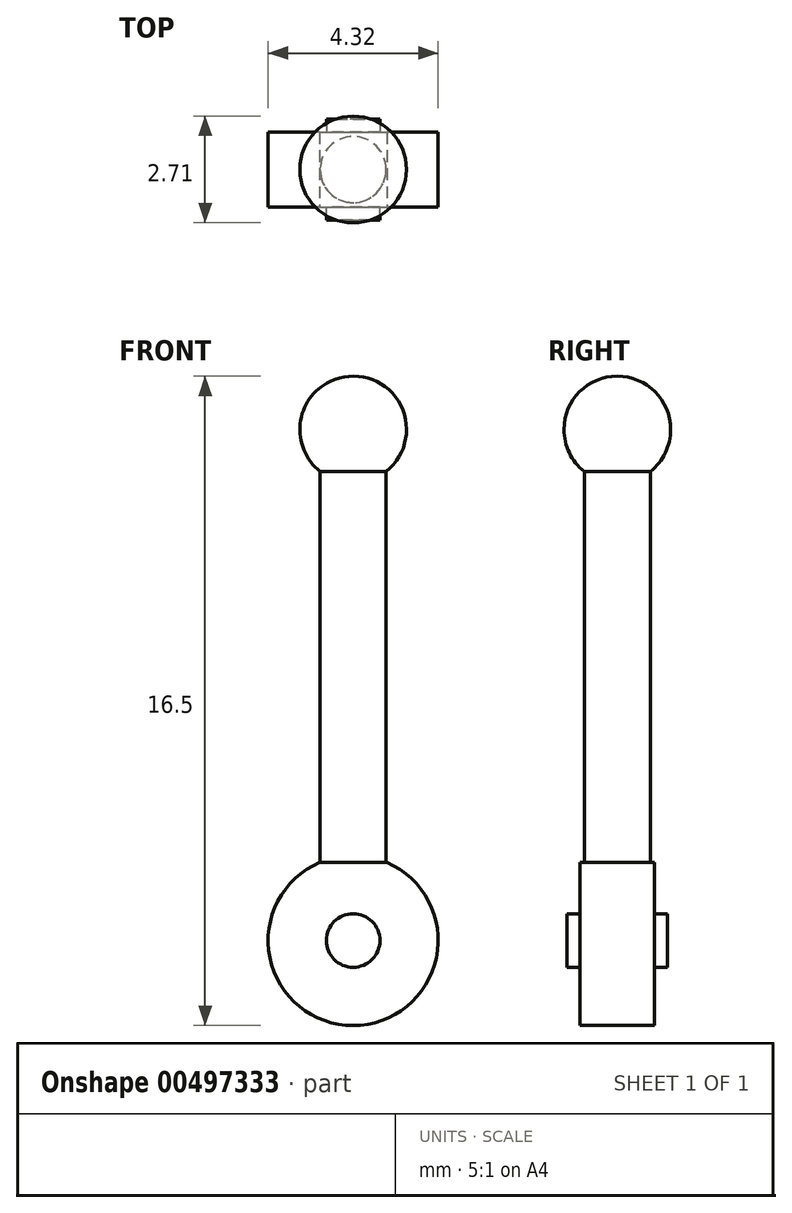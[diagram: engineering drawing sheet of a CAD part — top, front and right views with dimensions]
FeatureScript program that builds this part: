
annotation { "Feature Type Name" : "Feature", "Feature Type Description" : "" }
export const myFeature = defineFeature(function(context is Context, id is Id, definition is map)
    precondition{}
    {
        {
            var Q0;
            Q0=qCreatedBy(makeId("Front.planeOp"),FACE);
            var sketch = newSketch(context, id + "F0", { "sketchPlane" : qUnion([Q0])});
            skCircle(sketch, "E0", {"center": v(0, 0) * mm, "radius": 2.16 * mm});
            skSolve(sketch);
        }
        {
            var Q0;
            Q0 = qSketchRegion(id + "F0", true);
            extrude(context, id + "F1", {"entities" : qUnion([Q0]), "depth" : 1.9 * mm});
        }
        {
            var Q0;
            Q0=makeQuery(id+"F1.opExtrude","CAP_FACE",FACE,{"disambiguationData":[OSD([sQuery(id+"F0.wireOp",EDGE,"E0")])],"isStart":false});
            var sketch = newSketch(context, id + "F2", { "sketchPlane" : qUnion([Q0])});
            skLineSegment(sketch, "E1", {"start": v(-0.85, 1.98) * mm, "end": v(0.85, 1.98) * mm});
            skSolve(sketch);
        }
        {
            var Q0;
            Q0=makeQuery(id+"F1.opExtrude","CAP_FACE",FACE,{"disambiguationData":[OSD([sQuery(id+"F0.wireOp",EDGE,"E0")])],"isStart":true});
            var sketch = newSketch(context, id + "F3", { "sketchPlane" : qUnion([Q0])});
            skCircle(sketch, "E2", {"center": v(0, 0) * mm, "radius": 0.68 * mm});
            skSolve(sketch);
        }
        {
            var Q0;
            Q0 = qSketchRegion(id + "F3", true);
            extrude(context, id + "F4", {"entities" : qUnion([Q0]), "operationType" : NewBodyOperationType.ADD, "depth" : 0.33 * mm});
        }
        {
            var Q0;
            Q0=makeQuery(id+"F1.opExtrude","CAP_FACE",FACE,{"disambiguationData":[OSD([sQuery(id+"F0.wireOp",EDGE,"E0")])],"isStart":false});
            var sketch = newSketch(context, id + "F5", { "sketchPlane" : qUnion([Q0])});
            skCircle(sketch, "E3", {"center": v(0, 0) * mm, "radius": 0.68 * mm});
            skSolve(sketch);
        }
        {
            var Q0;
            Q0=makeQuery(id+"F5.imprint","IMPRINT",FACE,{"disambiguationData":[TD([[makeQuery(id+"F5.imprint","IMPRINT",EDGE,{"derivedFrom":sQuery(id+"F5.wireOp",EDGE,"E3")}),1.0]])]});
            extrude(context, id + "F6", {"entities" : qUnion([Q0]), "operationType" : NewBodyOperationType.ADD, "depth" : 0.33 * mm});
        }
        {
            var Q0;
            Q0 = qSketchRegion(id + "F2", true);
            var Q1;
            {var subQ0=sQuery(id+"F2.wireOp",EDGE,"E1");Q1=makeQuery(id+"F2.imprint","IMPRINT",FACE,{"disambiguationData":[TD([[makeQuery(id+"F2.imprint","IMPRINT",EDGE,{"derivedFrom":subQ0}),1.0]])]});}
            extrude(context, id + "F7", {"entities" : qUnion([Q0, Q1]), "operationType" : NewBodyOperationType.REMOVE, "oppositeDirection" : true, "depth" : 25 * mm});
        }
        {
            var Q0;
            Q0=makeQuery(id+"F7.boolean.opBoolean","COPY",FACE,{"derivedFrom":makeQuery(id+"F7.opExtrude","SWEPT_FACE",FACE,{"disambiguationData":[OSD([sQuery(id+"F2.wireOp",EDGE,"E1")])]})});
            var sketch = newSketch(context, id + "F8", { "sketchPlane" : qUnion([Q0])});
            skCircle(sketch, "E4", {"center": v(0, -0.95) * mm, "radius": 0.84 * mm});
            skPoint(sketch, "E4.centerSnap0", {"position": v(-0.85, -0.95) * mm});
            skPoint(sketch, "E4.centerSnap1", {"position": v(0, 0) * mm});
            skSolve(sketch);
        }
        {
            var Q0;
            Q0=makeQuery(id+"F8.imprint","IMPRINT",FACE,{"disambiguationData":[TD([[makeQuery(id+"F8.imprint","IMPRINT",EDGE,{"derivedFrom":sQuery(id+"F8.wireOp",EDGE,"E4")}),1.0]])]});
            extrude(context, id + "F9", {"entities" : qUnion([Q0]), "operationType" : NewBodyOperationType.ADD, "depth" : 11 * mm});
        }
        {
            var Q0;
            Q0=makeQuery(id+"F9.opExtrude","CAP_FACE",FACE,{"disambiguationData":[OSD([sQuery(id+"F8.wireOp",EDGE,"E4")])],"isStart":false});
            var sketch = newSketch(context, id + "F10", { "sketchPlane" : qUnion([Q0])});
            skArc(sketch, "E5", {"start": v(0, 0.4) * mm, "mid": v(-1.35, -0.95) * mm, "end": v(0, -2.3) * mm});
            skLineSegment(sketch, "E6", {"start": v(0, 0.4) * mm, "end": v(0, -2.3) * mm});
            skSolve(sketch);
        }
        {
            var Q0;
            Q0 = qSketchRegion(id + "F10", true);
            var Q1;
            {var subQ0=sQuery(id+"F10.wireOp",EDGE,"E5");Q1=makeQuery(id+"F10.imprint","IMPRINT",FACE,{"disambiguationData":[TD([[makeQuery(id+"F10.imprint","IMPRINT",EDGE,{"derivedFrom":subQ0}),1.0]])]});}
            var Q2;
            Q2=sQuery(id+"F10.wireOp",EDGE,"E6");
            revolve(context, id + "F11", {"operationType" : NewBodyOperationType.ADD, "entities" : qUnion([Q0, Q1]), "axis" : qUnion([Q2]), "revolveType" : RevolveType.FULL});
        }
    });
